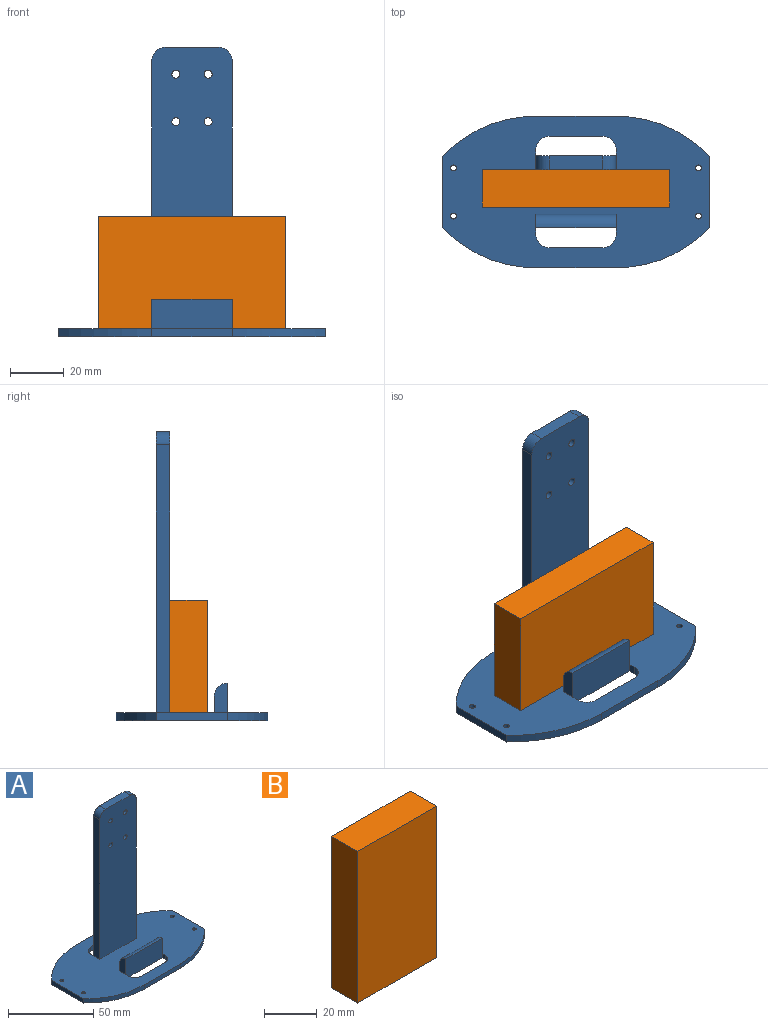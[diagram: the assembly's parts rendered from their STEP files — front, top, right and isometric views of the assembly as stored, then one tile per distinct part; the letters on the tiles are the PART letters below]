
ASSEMBLY  parts=2 mates=1
PART A: 40 faces, bbox 100x56.6x108 mm
  f0: plane 11x5mm, normal (-1,0,0), area 49.6mm2, adj f2,f14,f15,f39
  f1: plane 100x5mm, normal (1,0,0), area 500mm2, adj f10,f11,f13,f15
  f2: plane 30x14mm, normal (0,-1,0), area 420mm2, adj f0,f9,f20,f35,f38,f39
  f3: plane 20x5mm, normal (0,0,1), area 100mm2, adj f10,f11,f12,f13
  f4: plane 100x5mm, normal (-1,0,0), area 500mm2, adj f10,f11,f12,f15
  f5: cylinder r=1.5mm len=5mm, axis (0,1,0), area 47.1mm2, adj f10,f11
  f6: cylinder r=1.5mm len=5mm, axis (0,1,0), area 47.1mm2, adj f10,f11
  f7: cylinder r=1.5mm len=5mm, axis (0,1,0), area 47.1mm2, adj f10,f11
  f8: cylinder r=1.5mm len=5mm, axis (0,1,0), area 47.1mm2, adj f10,f11
  f9: plane 11x5mm, normal (1,0,0), area 49.6mm2, adj f2,f14,f15,f39
  f10: plane 105x30mm, normal (0,-1,0), area 3111mm2, adj f1,f3,f4,f5,f6,f7,f8,f12
  f11: plane 108x30mm, normal (0,1,0), area 3201mm2, adj f1,f3,f4,f5,f6,f7,f8,f12
  f12: cylinder r=5mm len=5mm, axis (0,-1,0), area 39.3mm2, adj f3,f4,f10,f11
  f13: cylinder r=5mm len=5mm, axis (0,1,0), area 39.3mm2, adj f1,f3,f10,f11
  f14: plane 30x6mm, normal (0,1,0), area 180mm2, adj f0,f9,f15,f39
  f15: plane 100x56.6mm, normal (0,0,1), area 4266.7mm2, adj f0,f1,f4,f9,f10,f14,f16,f17
  f16: plane 3x2.5mm, normal (1,0,0), area 7.5mm2, adj f11,f15,f34,f38
  f17: plane 3x2.5mm, normal (-1,0,0), area 7.5mm2, adj f11,f15,f18,f38
  f18: cylinder r=5mm len=5mm, axis (0,0,1), area 23.6mm2, adj f15,f17,f19,f38
  f19: plane 20x3mm, normal (0,-1,0), area 60mm2, adj f15,f18,f34,f38
  f20: plane 3x2.5mm, normal (1,0,0), area 7.5mm2, adj f2,f15,f21,f38
  f21: cylinder r=5mm len=5mm, axis (0,0,1), area 23.6mm2, adj f15,f20,f22,f38
  f22: plane 20x3mm, normal (0,1,0), area 60mm2, adj f15,f21,f23,f38
  f23: cylinder r=5mm len=5mm, axis (0,0,1), area 23.6mm2, adj f15,f22,f35,f38
  f24: cylinder r=48.33mm len=35mm, axis (0,0,1), area 117.4mm2, adj f15,f25,f36,f38
  f25: plane 26.6x3mm, normal (-1,0,0), area 79.8mm2, adj f15,f24,f26,f38
  f26: cylinder r=48.33mm len=35mm, axis (0,0,1), area 117.4mm2, adj f15,f25,f27,f38
  f27: plane 30x3mm, normal (0,1,0), area 90mm2, adj f15,f26,f28,f38
  f28: cylinder r=48.33mm len=35mm, axis (0,0,1), area 117.4mm2, adj f15,f27,f29,f38
  f29: plane 26.6x3mm, normal (1,0,0), area 79.8mm2, adj f15,f28,f30,f38
  f30: cylinder r=48.33mm len=35mm, axis (0,0,1), area 117.4mm2, adj f15,f29,f36,f38
  f31: cylinder r=1.09mm len=3mm, axis (0,0,1), area 20.5mm2, adj f15,f38
  f32: cylinder r=1.09mm len=3mm, axis (0,0,1), area 20.5mm2, adj f15,f38
  f33: cylinder r=1.09mm len=3mm, axis (0,0,1), area 20.5mm2, adj f15,f38
  f34: cylinder r=5mm len=5mm, axis (0,0,1), area 23.6mm2, adj f15,f16,f19,f38
  f35: plane 3x2.5mm, normal (-1,0,0), area 7.5mm2, adj f2,f15,f23,f38
  f36: plane 30x3mm, normal (0,-1,0), area 90mm2, adj f15,f24,f30,f38
  f37: cylinder r=1.09mm len=3mm, axis (0,0,1), area 20.5mm2, adj f15,f38
  f38: plane 100x56.6mm, normal (0,0,-1), area 4566.7mm2, adj f2,f11,f16,f17,f18,f19,f20,f21
  f39: cylinder r=5mm len=30mm, axis (-1,0,0), area 235.6mm2, adj f0,f2,f9,f14
PART B: 6 faces, bbox 42x14x70 mm
  f0: plane 70x14mm, normal (-1,0,0), area 980mm2, adj f1,f3,f4,f5
  f1: plane 42x14mm, normal (0,0,-1), area 588mm2, adj f0,f2,f4,f5
  f2: plane 70x14mm, normal (1,0,0), area 980mm2, adj f1,f3,f4,f5
  f3: plane 42x14mm, normal (0,0,1), area 588mm2, adj f0,f2,f4,f5
  f4: plane 70x42mm, normal (0,-1,0), area 2940mm2, adj f0,f1,f2,f3
  f5: plane 70x42mm, normal (0,1,0), area 2940mm2, adj f0,f1,f2,f3
PLACE A t=(11.19,-68.28,20.63)mm
PLACE B rot(axis=(0,1,0),90deg) t=(3,-73.28,13.36)mm
MATE fastened A.f10 <-> B.f5  axis (0,-1,0) through (38,-73.28,-28.64)mm
